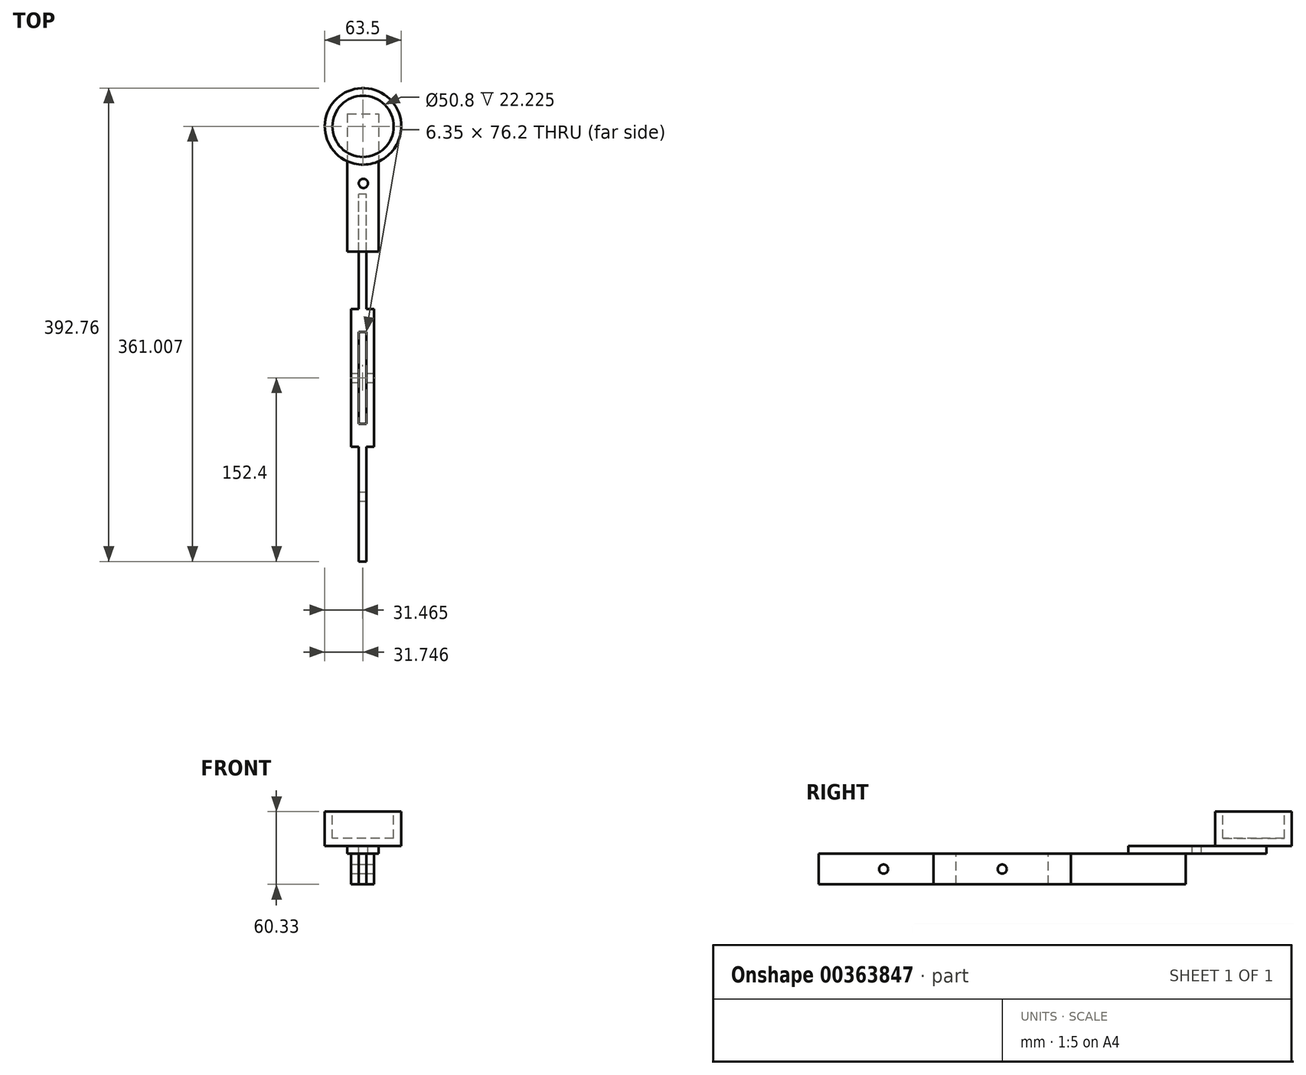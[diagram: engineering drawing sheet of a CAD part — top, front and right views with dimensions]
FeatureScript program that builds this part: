
annotation { "Feature Type Name" : "Feature", "Feature Type Description" : "" }
export const myFeature = defineFeature(function(context is Context, id is Id, definition is map)
    precondition{}
    {
        {
            var Q0;
            Q0=qCreatedBy(makeId("Right.planeOp"),FACE);
            var sketch = newSketch(context, id + "F0", { "sketchPlane" : qUnion([Q0])});
            skLineSegment(sketch, "E0.bottom", {"start": v(0, 0) * mm, "end": v(304.8, 0) * mm});
            skLineSegment(sketch, "E0.top", {"start": v(0, 25.4) * mm, "end": v(304.8, 25.4) * mm});
            skLineSegment(sketch, "E0.left", {"start": v(0, 0) * mm, "end": v(0, 25.4) * mm});
            skLineSegment(sketch, "E0.right", {"start": v(304.8, 0) * mm, "end": v(304.8, 25.4) * mm});
            skSolve(sketch);
        }
        {
            var Q0;
            Q0 = qSketchRegion(id + "F0", true);
            extrude(context, id + "F1", {"entities" : qUnion([Q0]), "depth" : 19.05 * mm});
        }
        {
            var Q0;
            Q0=makeQuery(id+"F1.opExtrude","CAP_FACE",FACE,{"disambiguationData":[OSD([sQuery(id+"F0.wireOp",EDGE,"E0.bottom"),sQuery(id+"F0.wireOp",EDGE,"E0.top"),sQuery(id+"F0.wireOp",EDGE,"E0.left"),sQuery(id+"F0.wireOp",EDGE,"E0.right")])],"isStart":false});
            var sketch = newSketch(context, id + "F2", { "sketchPlane" : qUnion([Q0])});
            skLineSegment(sketch, "E1.bottom", {"start": v(0, 0) * mm, "end": v(95.25, 0) * mm});
            skLineSegment(sketch, "E1.top", {"start": v(0, 25.4) * mm, "end": v(95.25, 25.4) * mm});
            skLineSegment(sketch, "E1.left", {"start": v(0, 0) * mm, "end": v(0, 25.4) * mm});
            skLineSegment(sketch, "E1.right", {"start": v(95.25, 0) * mm, "end": v(95.25, 25.4) * mm});
            skSolve(sketch);
        }
        {
            var Q0;
            Q0 = qSketchRegion(id + "F2", true);
            extrude(context, id + "F3", {"entities" : qUnion([Q0]), "operationType" : NewBodyOperationType.REMOVE, "oppositeDirection" : true, "depth" : 6.35 * mm});
        }
        {
            var Q0;
            Q0=makeQuery(id+"F1.opExtrude","CAP_FACE",FACE,{"disambiguationData":[OSD([sQuery(id+"F0.wireOp",EDGE,"E0.bottom"),sQuery(id+"F0.wireOp",EDGE,"E0.top"),sQuery(id+"F0.wireOp",EDGE,"E0.left"),sQuery(id+"F0.wireOp",EDGE,"E0.right")])],"isStart":true});
            var sketch = newSketch(context, id + "F4", { "sketchPlane" : qUnion([Q0])});
            skLineSegment(sketch, "E2.bottom", {"start": v(0, 25.4) * mm, "end": v(-95.25, 25.4) * mm});
            skLineSegment(sketch, "E2.top", {"start": v(0, 0) * mm, "end": v(-95.25, 0) * mm});
            skLineSegment(sketch, "E2.left", {"start": v(0, 25.4) * mm, "end": v(0, 0) * mm});
            skLineSegment(sketch, "E2.right", {"start": v(-95.25, 25.4) * mm, "end": v(-95.25, 0) * mm});
            skSolve(sketch);
        }
        {
            var Q0;
            Q0=makeQuery(id+"F4.imprint","IMPRINT",FACE,{"disambiguationData":[TD([[makeQuery(id+"F4.imprint","IMPRINT",EDGE,{"derivedFrom":sQuery(id+"F4.wireOp",EDGE,"E2.bottom")}),1.0]])]});
            extrude(context, id + "F5", {"entities" : qUnion([Q0]), "operationType" : NewBodyOperationType.REMOVE, "oppositeDirection" : true, "depth" : 6.35 * mm});
        }
        {
            var Q0;
            Q0=makeQuery(id+"F1.opExtrude","CAP_FACE",FACE,{"disambiguationData":[OSD([sQuery(id+"F0.wireOp",EDGE,"E0.bottom"),sQuery(id+"F0.wireOp",EDGE,"E0.top"),sQuery(id+"F0.wireOp",EDGE,"E0.left"),sQuery(id+"F0.wireOp",EDGE,"E0.right")])],"isStart":false});
            var sketch = newSketch(context, id + "F6", { "sketchPlane" : qUnion([Q0])});
            skLineSegment(sketch, "E3.bottom", {"start": v(304.8, 25.4) * mm, "end": v(209.55, 25.4) * mm});
            skLineSegment(sketch, "E3.top", {"start": v(304.8, 0) * mm, "end": v(209.55, 0) * mm});
            skLineSegment(sketch, "E3.left", {"start": v(304.8, 25.4) * mm, "end": v(304.8, 0) * mm});
            skLineSegment(sketch, "E3.right", {"start": v(209.55, 25.4) * mm, "end": v(209.55, 0) * mm});
            skSolve(sketch);
        }
        {
            var Q0;
            Q0 = qSketchRegion(id + "F6", true);
            extrude(context, id + "F7", {"entities" : qUnion([Q0]), "operationType" : NewBodyOperationType.REMOVE, "oppositeDirection" : true, "depth" : 6.35 * mm});
        }
        {
            var Q0;
            Q0=makeQuery(id+"F1.opExtrude","CAP_FACE",FACE,{"disambiguationData":[OSD([sQuery(id+"F0.wireOp",EDGE,"E0.bottom"),sQuery(id+"F0.wireOp",EDGE,"E0.top"),sQuery(id+"F0.wireOp",EDGE,"E0.left"),sQuery(id+"F0.wireOp",EDGE,"E0.right")])],"isStart":true});
            var sketch = newSketch(context, id + "F8", { "sketchPlane" : qUnion([Q0])});
            skLineSegment(sketch, "E4.bottom", {"start": v(-304.8, 0) * mm, "end": v(-209.55, 0) * mm});
            skLineSegment(sketch, "E4.top", {"start": v(-304.8, 25.4) * mm, "end": v(-209.55, 25.4) * mm});
            skLineSegment(sketch, "E4.left", {"start": v(-304.8, 0) * mm, "end": v(-304.8, 25.4) * mm});
            skLineSegment(sketch, "E4.right", {"start": v(-209.55, 0) * mm, "end": v(-209.55, 25.4) * mm});
            skSolve(sketch);
        }
        {
            var Q0;
            Q0 = qSketchRegion(id + "F8", true);
            extrude(context, id + "F9", {"entities" : qUnion([Q0]), "operationType" : NewBodyOperationType.REMOVE, "oppositeDirection" : true, "depth" : 6.35 * mm});
        }
        {
            var Q0;
            Q0=makeQuery(id+"F1.opExtrude","SWEPT_FACE",FACE,{"disambiguationData":[OSD([sQuery(id+"F0.wireOp",EDGE,"E0.top")])]});
            var sketch = newSketch(context, id + "F10", { "sketchPlane" : qUnion([Q0])});
            skLineSegment(sketch, "E5.bottom", {"start": v(6.35, 190.5) * mm, "end": v(12.7, 190.5) * mm});
            skLineSegment(sketch, "E5.top", {"start": v(6.35, 114.3) * mm, "end": v(12.7, 114.3) * mm});
            skLineSegment(sketch, "E5.left", {"start": v(6.35, 190.5) * mm, "end": v(6.35, 114.3) * mm});
            skLineSegment(sketch, "E5.right", {"start": v(12.7, 190.5) * mm, "end": v(12.7, 114.3) * mm});
            skSolve(sketch);
        }
        {
            var Q0;
            Q0 = qSketchRegion(id + "F10", true);
            extrude(context, id + "F11", {"entities" : qUnion([Q0]), "operationType" : NewBodyOperationType.REMOVE, "oppositeDirection" : true, "depth" : 25.4 * mm});
        }
        {
            var Q0;
            Q0=makeQuery(id+"F1.opExtrude","CAP_FACE",FACE,{"disambiguationData":[OSD([sQuery(id+"F0.wireOp",EDGE,"E0.bottom"),sQuery(id+"F0.wireOp",EDGE,"E0.top"),sQuery(id+"F0.wireOp",EDGE,"E0.left"),sQuery(id+"F0.wireOp",EDGE,"E0.right")])],"isStart":false});
            var sketch = newSketch(context, id + "F12", { "sketchPlane" : qUnion([Q0])});
            skCircle(sketch, "E6", {"center": v(152.4, 12.7) * mm, "radius": 3.81 * mm});
            skPoint(sketch, "E6.centerSnap0", {"position": v(152.4, 25.4) * mm});
            skSolve(sketch);
        }
        {
            var Q0;
            Q0 = qSketchRegion(id + "F12", true);
            extrude(context, id + "F13", {"entities" : qUnion([Q0]), "operationType" : NewBodyOperationType.REMOVE, "oppositeDirection" : true, "depth" : 25.4 * mm});
        }
        {
            var Q0;
            Q0=makeQuery(id+"F1.opExtrude","SWEPT_FACE",FACE,{"disambiguationData":[OSD([sQuery(id+"F0.wireOp",EDGE,"E0.top")])]});
            var sketch = newSketch(context, id + "F14", { "sketchPlane" : qUnion([Q0])});
            skLineSegment(sketch, "E7.bottom", {"start": v(-3.18, 371.48) * mm, "end": v(22.79, 371.48) * mm});
            skLineSegment(sketch, "E7.top", {"start": v(-3.17, 257.18) * mm, "end": v(22.79, 257.18) * mm});
            skLineSegment(sketch, "E7.left", {"start": v(-3.18, 371.48) * mm, "end": v(-3.17, 257.18) * mm});
            skLineSegment(sketch, "E7.right", {"start": v(22.79, 371.48) * mm, "end": v(22.79, 257.18) * mm});
            skSolve(sketch);
        }
        {
            var Q0;
            Q0 = qSketchRegion(id + "F14", true);
            extrude(context, id + "F15", {"entities" : qUnion([Q0]), "operationType" : NewBodyOperationType.ADD, "depth" : 6.35 * mm});
        }
        {
            var Q0;
            Q0=makeQuery(id+"F15.opExtrude","CAP_FACE",FACE,{"disambiguationData":[OSD([sQuery(id+"F14.wireOp",EDGE,"E7.bottom"),sQuery(id+"F14.wireOp",EDGE,"E7.top"),sQuery(id+"F14.wireOp",EDGE,"E7.left"),sQuery(id+"F14.wireOp",EDGE,"E7.right")])],"isStart":false});
            var sketch = newSketch(context, id + "F16", { "sketchPlane" : qUnion([Q0])});
            skCircle(sketch, "E8", {"center": v(10.09, 313.7) * mm, "radius": 3.81 * mm});
            skSolve(sketch);
        }
        {
            var Q0;
            Q0 = qSketchRegion(id + "F16", true);
            extrude(context, id + "F17", {"entities" : qUnion([Q0]), "operationType" : NewBodyOperationType.REMOVE, "oppositeDirection" : true, "depth" : 25.4 * mm});
        }
        {
            var Q0;
            Q0=makeQuery(id+"F3.boolean.opBoolean","COPY",FACE,{"derivedFrom":makeQuery(id+"F3.opExtrude","CAP_FACE",FACE,{"disambiguationData":[OSD([sQuery(id+"F2.wireOp",EDGE,"E1.bottom"),sQuery(id+"F2.wireOp",EDGE,"E1.top"),sQuery(id+"F2.wireOp",EDGE,"E1.left"),sQuery(id+"F2.wireOp",EDGE,"E1.right")])],"isStart":false})});
            var sketch = newSketch(context, id + "F18", { "sketchPlane" : qUnion([Q0])});
            skCircle(sketch, "E9", {"center": v(53.98, 12.7) * mm, "radius": 3.8 * mm});
            skSolve(sketch);
        }
        {
            var Q0;
            Q0 = qSketchRegion(id + "F18", true);
            extrude(context, id + "F19", {"entities" : qUnion([Q0]), "operationType" : NewBodyOperationType.REMOVE, "oppositeDirection" : true, "depth" : 25.4 * mm});
        }
        {
            var Q0;
            Q0=makeQuery(id+"F15.opExtrude","CAP_FACE",FACE,{"disambiguationData":[OSD([sQuery(id+"F14.wireOp",EDGE,"E7.bottom"),sQuery(id+"F14.wireOp",EDGE,"E7.top"),sQuery(id+"F14.wireOp",EDGE,"E7.left"),sQuery(id+"F14.wireOp",EDGE,"E7.right")])],"isStart":false});
            var sketch = newSketch(context, id + "F20", { "sketchPlane" : qUnion([Q0])});
            skCircle(sketch, "E10", {"center": v(9.8, 361) * mm, "radius": 31.75 * mm});
            skPoint(sketch, "E10.centerSnap0", {"position": v(9.8, 257.18) * mm});
            skSolve(sketch);
        }
        {
            var Q0;
            Q0 = qSketchRegion(id + "F20", true);
            extrude(context, id + "F21", {"entities" : qUnion([Q0]), "operationType" : NewBodyOperationType.ADD, "depth" : 28.57 * mm});
        }
        {
            var Q0;
            Q0=makeQuery(id+"F21.opExtrude","CAP_FACE",FACE,{"disambiguationData":[OSD([sQuery(id+"F20.wireOp",EDGE,"E10")])],"isStart":false});
            var sketch = newSketch(context, id + "F22", { "sketchPlane" : qUnion([Q0])});
            skCircle(sketch, "E11", {"center": v(9.8, 361) * mm, "radius": 25.4 * mm});
            skSolve(sketch);
        }
        {
            var Q0;
            Q0 = qSketchRegion(id + "F22", true);
            extrude(context, id + "F23", {"entities" : qUnion([Q0]), "operationType" : NewBodyOperationType.REMOVE, "oppositeDirection" : true, "depth" : 22.22 * mm});
        }
    });
